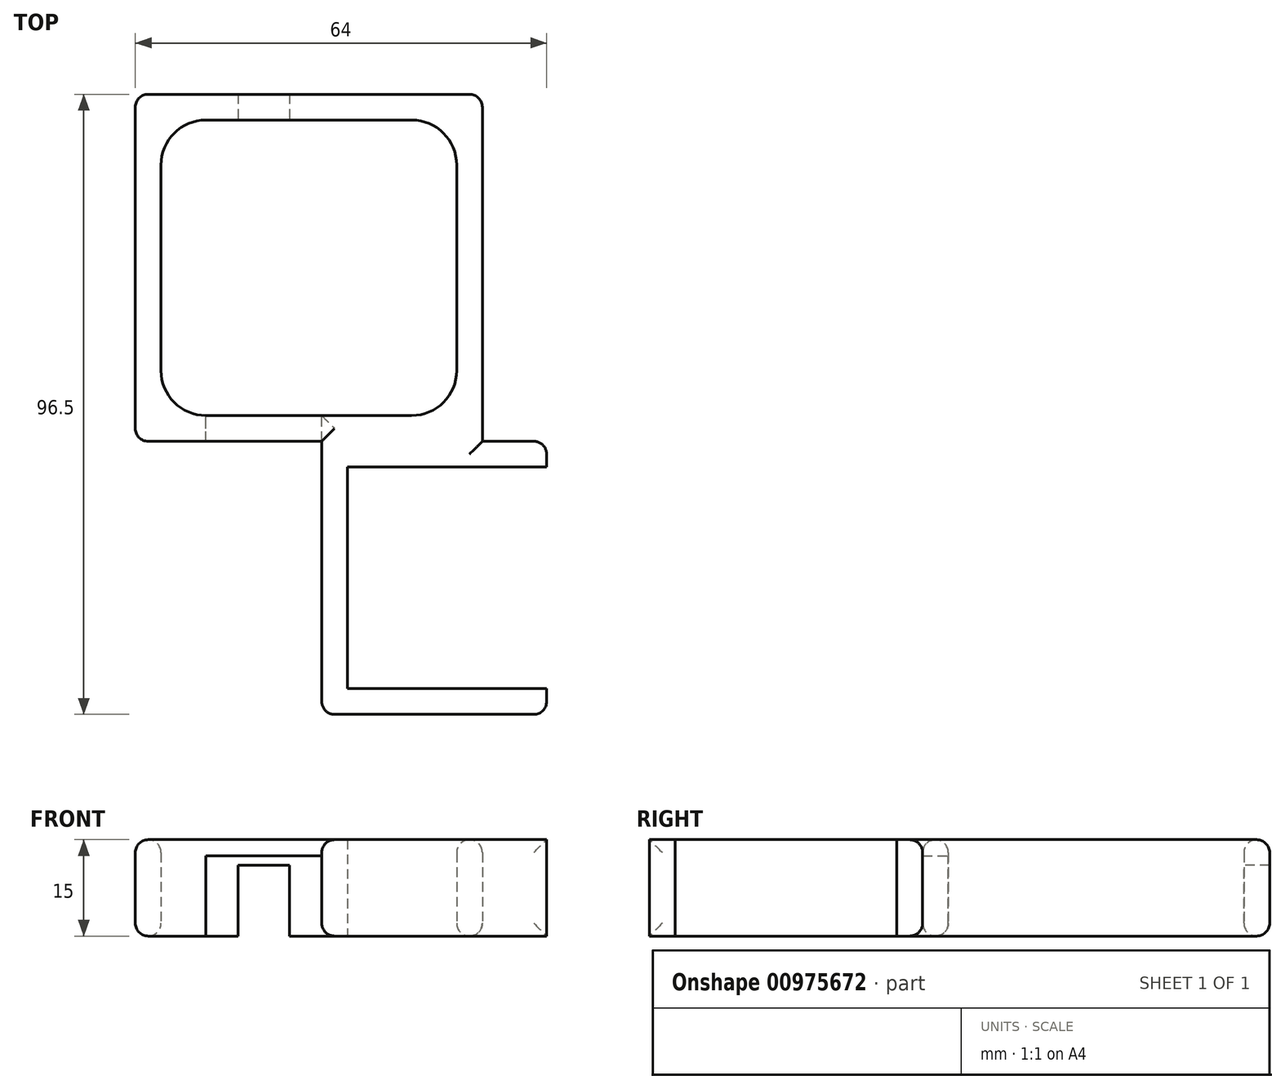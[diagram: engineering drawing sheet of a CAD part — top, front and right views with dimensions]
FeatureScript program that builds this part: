
annotation { "Feature Type Name" : "Feature", "Feature Type Description" : "" }
export const myFeature = defineFeature(function(context is Context, id is Id, definition is map)
    precondition{}
    {
        {
            var Q0;
            Q0=qCreatedBy(makeId("Top.planeOp"),FACE);
            var sketch = newSketch(context, id + "F0", { "sketchPlane" : qUnion([Q0])});
            skLineSegment(sketch, "E0", {"start": v(29.47, 14.54) * mm, "end": v(29.47, 10.54) * mm});
            skLineSegment(sketch, "E1", {"start": v(29.47, 10.54) * mm, "end": v(-1.53, 10.54) * mm});
            skLineSegment(sketch, "E2", {"start": v(-1.53, 10.54) * mm, "end": v(-1.53, -23.96) * mm});
            skLineSegment(sketch, "E3", {"start": v(-1.53, -23.96) * mm, "end": v(29.47, -23.96) * mm});
            skLineSegment(sketch, "E4", {"start": v(29.47, -23.96) * mm, "end": v(29.47, -27.96) * mm});
            skLineSegment(sketch, "E5", {"start": v(29.47, -27.96) * mm, "end": v(-5.53, -27.96) * mm});
            skLineSegment(sketch, "E6", {"start": v(-5.53, -27.96) * mm, "end": v(-5.53, 14.54) * mm});
            skLineSegment(sketch, "E7", {"start": v(-5.53, 14.54) * mm, "end": v(29.47, 14.54) * mm});
            skLineSegment(sketch, "E8.bottom", {"start": v(29.47, -23.96) * mm, "end": v(27.47, -23.96) * mm});
            skLineSegment(sketch, "E9.bottom", {"start": v(29.47, 10.54) * mm, "end": v(27.47, 10.54) * mm});
            skPoint(sketch, "E10", {"position": v(-5.53, -6.71) * mm});
            skSolve(sketch);
        }
        {
            var Q0;
            Q0 = qSketchRegion(id + "F0", true);
            extrude(context, id + "F1", {"entities" : qUnion([Q0]), "endBound" : BoundingType.SYMMETRIC, "depth" : 15 * mm, "offsetDistance" : 25 * mm});
        }
        {
            var Q0;
            Q0=qCreatedBy(makeId("Top.planeOp"),FACE);
            var sketch = newSketch(context, id + "F2", { "sketchPlane" : qUnion([Q0])});
            skPoint(sketch, "E11.0", {"position": v(-5.53, 14.54) * mm});
            skPoint(sketch, "E12.0", {"position": v(29.47, 14.54) * mm});
            skLineSegment(sketch, "E13.bottom", {"start": v(-30.53, 64.54) * mm, "end": v(-18.53, 64.54) * mm});
            skLineSegment(sketch, "E13.top", {"start": v(-30.53, 18.54) * mm, "end": v(-23.53, 18.54) * mm});
            skLineSegment(sketch, "E13.left", {"start": v(-30.53, 64.54) * mm, "end": v(-30.53, 18.54) * mm});
            skLineSegment(sketch, "E13.right", {"start": v(15.47, 64.54) * mm, "end": v(15.47, 18.54) * mm});
            skLineSegment(sketch, "E14.0", {"start": v(-34.53, 68.54) * mm, "end": v(-18.53, 68.54) * mm});
            skLineSegment(sketch, "E14.1", {"start": v(-34.53, 68.54) * mm, "end": v(-34.53, 14.54) * mm});
            skLineSegment(sketch, "E14.2", {"start": v(-34.53, 14.54) * mm, "end": v(-23.53, 14.54) * mm});
            skLineSegment(sketch, "E14.3", {"start": v(19.47, 68.54) * mm, "end": v(19.47, 14.54) * mm});
            skLineSegment(sketch, "E15", {"start": v(-5.53, 14.54) * mm, "end": v(-5.53, 18.54) * mm});
            skLineSegment(sketch, "E16.MirrorCS", {"start": v(-23.53, 14.54) * mm, "end": v(-23.53, 18.54) * mm});
            skLineSegment(sketch, "E17", {"start": v(-18.53, 79.1) * mm, "end": v(-18.53, 29.22) * mm});
            skLineSegment(sketch, "E18", {"start": v(-10.53, 79.84) * mm, "end": v(-10.53, 54.16) * mm});
            skLineSegment(sketch, "E19.trimOffspring", {"start": v(-10.53, 68.54) * mm, "end": v(19.47, 68.54) * mm});
            skLineSegment(sketch, "E20.trimOffspring", {"start": v(-10.53, 64.54) * mm, "end": v(15.47, 64.54) * mm});
            skLineSegment(sketch, "E21.trimOffspring", {"start": v(-5.53, 18.54) * mm, "end": v(15.47, 18.54) * mm});
            skLineSegment(sketch, "E22.trimOffspring", {"start": v(-5.53, 14.54) * mm, "end": v(19.47, 14.54) * mm});
            skLineSegment(sketch, "E23", {"start": v(-23.53, 14.54) * mm, "end": v(-5.53, 14.54) * mm});
            skLineSegment(sketch, "E24", {"start": v(-23.53, 18.54) * mm, "end": v(-5.53, 18.54) * mm});
            skLineSegment(sketch, "E25", {"start": v(-18.53, 68.54) * mm, "end": v(-10.53, 68.54) * mm});
            skLineSegment(sketch, "E26", {"start": v(-10.53, 64.54) * mm, "end": v(-18.53, 64.54) * mm});
            skSolve(sketch);
        }
        {
            var Q0;
            {var subQ1=sQuery(id+"F2.wireOp",EDGE,"E13.bottom");Q0=makeQuery(id+"F2.imprint","IMPRINT",FACE,{"disambiguationData":[TD([[makeQuery(id+"F2.imprint","IMPRINT",EDGE,{"derivedFrom":subQ1}),1.0]])]});}
            var Q1;
            Q1=makeQuery(id+"F2.imprint","IMPRINT",FACE,{"disambiguationData":[TD([[makeQuery(id+"F2.imprint","IMPRINT",EDGE,{"derivedFrom":sQuery(id+"F2.wireOp",EDGE,"E13.right")}),1.0]])]});
            var Q2;
            Q2=makeQuery(id+"F2.imprint","IMPRINT",FACE,{"disambiguationData":[TD([[makeQuery(id+"F2.imprint","IMPRINT",EDGE,{"derivedFrom":sQuery(id+"F2.wireOp",EDGE,"E15")}),1.0]])]});
            var Q3;
            {var subQ2=sQuery(id+"F2.wireOp",EDGE,"E25");Q3=makeQuery(id+"F2.imprint","IMPRINT",FACE,{"disambiguationData":[TD([[makeQuery(id+"F2.imprint","IMPRINT",EDGE,{"derivedFrom":subQ2}),-1.0]])]});}
            extrude(context, id + "F3", {"entities" : qUnion([Q0, Q1, Q2, Q3]), "operationType" : NewBodyOperationType.ADD, "endBound" : BoundingType.SYMMETRIC, "depth" : 15 * mm, "offsetDistance" : 25 * mm});
        }
        {
            var Q0;
            Q0=makeQuery(id+"F2.imprint","IMPRINT",FACE,{"disambiguationData":[TD([[makeQuery(id+"F2.imprint","IMPRINT",EDGE,{"derivedFrom":sQuery(id+"F2.wireOp",EDGE,"E15")}),1.0]])]});
            extrude(context, id + "F4", {"entities" : qUnion([Q0]), "operationType" : NewBodyOperationType.REMOVE, "endBound" : BoundingType.SYMMETRIC, "oppositeDirection" : true, "depth" : 10 * mm, "offsetDistance" : 25 * mm});
        }
        {
            var Q0;
            Q0=makeQuery(id+"F2.imprint","IMPRINT",FACE,{"disambiguationData":[TD([[makeQuery(id+"F2.imprint","IMPRINT",EDGE,{"derivedFrom":sQuery(id+"F2.wireOp",EDGE,"E15")}),1.0]])]});
            extrude(context, id + "F5", {"entities" : qUnion([Q0]), "operationType" : NewBodyOperationType.REMOVE, "oppositeDirection" : true, "depth" : 25 * mm, "offsetDistance" : 25 * mm});
        }
        {
            var Q0;
            {var subQ2=sQuery(id+"F2.wireOp",EDGE,"E25");Q0=makeQuery(id+"F2.imprint","IMPRINT",FACE,{"disambiguationData":[TD([[makeQuery(id+"F2.imprint","IMPRINT",EDGE,{"derivedFrom":subQ2}),-1.0]])]});}
            extrude(context, id + "F6", {"entities" : qUnion([Q0]), "operationType" : NewBodyOperationType.REMOVE, "endBound" : BoundingType.SYMMETRIC, "oppositeDirection" : true, "depth" : 7 * mm, "offsetDistance" : 25 * mm});
        }
        {
            var Q0;
            {var subQ2=sQuery(id+"F2.wireOp",EDGE,"E25");Q0=makeQuery(id+"F2.imprint","IMPRINT",FACE,{"disambiguationData":[TD([[makeQuery(id+"F2.imprint","IMPRINT",EDGE,{"derivedFrom":subQ2}),-1.0]])]});}
            extrude(context, id + "F7", {"entities" : qUnion([Q0]), "operationType" : NewBodyOperationType.REMOVE, "oppositeDirection" : true, "depth" : 25 * mm, "offsetDistance" : 25 * mm});
        }
        {
            var Q0;
            Q0=makeQuery(id+"F3.opExtrude","SWEPT_EDGE",EDGE,{"disambiguationData":[OSD([sQuery(id+"F2.wireOp",EDGE,"E13.bottom"),sQuery(id+"F2.wireOp",EDGE,"E13.left")])]});
            var Q1;
            Q1=makeQuery(id+"F3.opExtrude","SWEPT_EDGE",EDGE,{"disambiguationData":[OSD([sQuery(id+"F2.wireOp",EDGE,"E13.right"),sQuery(id+"F2.wireOp",EDGE,"E20.trimOffspring")])]});
            var Q2;
            Q2=makeQuery(id+"F3.opExtrude","SWEPT_EDGE",EDGE,{"disambiguationData":[OSD([sQuery(id+"F2.wireOp",EDGE,"E13.top"),sQuery(id+"F2.wireOp",EDGE,"E13.left")])]});
            var Q3;
            Q3=makeQuery(id+"F3.opExtrude","SWEPT_EDGE",EDGE,{"disambiguationData":[OSD([sQuery(id+"F2.wireOp",EDGE,"E13.right"),sQuery(id+"F2.wireOp",EDGE,"E21.trimOffspring")])]});
            fillet(context, id + "F8", {"entities" : qUnion([Q0, Q1, Q2, Q3]), "radius" : 7 * mm, "tangentPropagation" : true, "defaultsChanged" : true, "vertexSettings" : [], "allowEdgeOverflow" : false});
        }
        {
            var Q0;
            Q0=makeQuery(id+"F3.opExtrude","CAP_EDGE",EDGE,{"disambiguationData":[OSD([sQuery(id+"F2.wireOp",EDGE,"E14.3")])],"isStart":false});
            var Q1;
            Q1=makeQuery(id+"F3.opExtrude","CAP_EDGE",EDGE,{"disambiguationData":[OSD([sQuery(id+"F2.wireOp",EDGE,"E14.3")])],"isStart":true});
            var Q2;
            Q2=makeQuery(id+"F1.opExtrude","CAP_EDGE",EDGE,{"disambiguationData":[OSD([sQuery(id+"F0.wireOp",EDGE,"E7")])],"isStart":false});
            var Q3;
            Q3=makeQuery(id+"F1.opExtrude","CAP_EDGE",EDGE,{"disambiguationData":[OSD([sQuery(id+"F0.wireOp",EDGE,"E7")])],"isStart":true});
            var Q4;
            Q4=makeQuery(id+"F3.opExtrude","SWEPT_EDGE",EDGE,{"disambiguationData":[OSD([sQuery(id+"F2.wireOp",EDGE,"E14.3"),sQuery(id+"F2.wireOp",EDGE,"E19.trimOffspring")])]});
            var Q5;
            {var subQ0=sQuery(id+"F2.wireOp",EDGE,"E14.3");var subQ2=sQuery(id+"F2.wireOp",EDGE,"E25");var subQ3=sQuery(id+"F2.wireOp",EDGE,"E19.trimOffspring");var subQ4=sQuery(id+"F2.wireOp",EDGE,"E14.0");Q5=makeQuery(id+"F7.boolean.opBoolean","SPLIT",EDGE,{"disambiguationData":[TD([makeQuery(id+"F3.opExtrude","SWEPT_FACE",FACE,{"disambiguationData":[OSD([subQ0])]})])],"derivedFrom":makeQuery(id+"F3.opExtrude","CAP_EDGE",EDGE,{"disambiguationData":[OSD([subQ4,subQ3,subQ2])],"isStart":true})});}
            var Q6;
            Q6=makeQuery(id+"F3.opExtrude","CAP_EDGE",EDGE,{"disambiguationData":[OSD([sQuery(id+"F2.wireOp",EDGE,"E14.0"),sQuery(id+"F2.wireOp",EDGE,"E19.trimOffspring"),sQuery(id+"F2.wireOp",EDGE,"E25")])],"isStart":false});
            var Q7;
            Q7=makeQuery(id+"F6.boolean.opBoolean","COPY",EDGE,{"derivedFrom":makeQuery(id+"F6.opExtrude","CAP_EDGE",EDGE,{"disambiguationData":[OSD([sQuery(id+"F2.wireOp",EDGE,"E25")])],"isStart":true})});
            var Q8;
            {var subQ0=sQuery(id+"F2.wireOp",EDGE,"E25");var subQ1=sQuery(id+"F2.wireOp",EDGE,"E17");var subQ2=sQuery(id+"F2.wireOp",EDGE,"E14.0");Q8=makeQuery(id+"F7.boolean.opBoolean","MERGE",EDGE,{"derivedFrom":[makeQuery(id+"F6.boolean.opBoolean","COPY",EDGE,{"derivedFrom":makeQuery(id+"F6.opExtrude","SWEPT_EDGE",EDGE,{"disambiguationData":[OSD([subQ2,subQ1,subQ0])]})})],"fromTools":[makeQuery(id+"F7.opExtrude","SWEPT_EDGE",EDGE,{"disambiguationData":[OSD([subQ2,subQ1,subQ0])]})]});}
            var Q9;
            {var subQ0=sQuery(id+"F2.wireOp",EDGE,"E25");var subQ1=sQuery(id+"F2.wireOp",EDGE,"E19.trimOffspring");var subQ2=sQuery(id+"F2.wireOp",EDGE,"E18");Q9=makeQuery(id+"F7.boolean.opBoolean","MERGE",EDGE,{"derivedFrom":[makeQuery(id+"F6.boolean.opBoolean","COPY",EDGE,{"derivedFrom":makeQuery(id+"F6.opExtrude","SWEPT_EDGE",EDGE,{"disambiguationData":[OSD([subQ2,subQ1,subQ0])]})})],"fromTools":[makeQuery(id+"F7.opExtrude","SWEPT_EDGE",EDGE,{"disambiguationData":[OSD([subQ2,subQ1,subQ0])]})]});}
            var Q10;
            {var subQ0=sQuery(id+"F2.wireOp",EDGE,"E26");var subQ1=sQuery(id+"F2.wireOp",EDGE,"E20.trimOffspring");var subQ2=sQuery(id+"F2.wireOp",EDGE,"E18");Q10=makeQuery(id+"F7.boolean.opBoolean","MERGE",EDGE,{"derivedFrom":[makeQuery(id+"F6.boolean.opBoolean","COPY",EDGE,{"derivedFrom":makeQuery(id+"F6.opExtrude","SWEPT_EDGE",EDGE,{"disambiguationData":[OSD([subQ2,subQ1,subQ0])]})})],"fromTools":[makeQuery(id+"F7.opExtrude","SWEPT_EDGE",EDGE,{"disambiguationData":[OSD([subQ2,subQ1,subQ0])]})]});}
            var Q11;
            {var subQ0=sQuery(id+"F2.wireOp",EDGE,"E26");var subQ1=sQuery(id+"F2.wireOp",EDGE,"E17");var subQ2=sQuery(id+"F2.wireOp",EDGE,"E13.bottom");Q11=makeQuery(id+"F7.boolean.opBoolean","MERGE",EDGE,{"derivedFrom":[makeQuery(id+"F6.boolean.opBoolean","COPY",EDGE,{"derivedFrom":makeQuery(id+"F6.opExtrude","SWEPT_EDGE",EDGE,{"disambiguationData":[OSD([subQ2,subQ1,subQ0])]})})],"fromTools":[makeQuery(id+"F7.opExtrude","SWEPT_EDGE",EDGE,{"disambiguationData":[OSD([subQ2,subQ1,subQ0])]})]});}
            var Q12;
            Q12=makeQuery(id+"F3.opExtrude","SWEPT_EDGE",EDGE,{"disambiguationData":[OSD([sQuery(id+"F2.wireOp",EDGE,"E14.0"),sQuery(id+"F2.wireOp",EDGE,"E14.1")])]});
            var Q13;
            {var subQ0=sQuery(id+"F2.wireOp",EDGE,"E14.1");var subQ1=sQuery(id+"F2.wireOp",EDGE,"E25");var subQ2=sQuery(id+"F2.wireOp",EDGE,"E19.trimOffspring");var subQ3=sQuery(id+"F2.wireOp",EDGE,"E14.0");Q13=makeQuery(id+"F7.boolean.opBoolean","SPLIT",EDGE,{"disambiguationData":[TD([makeQuery(id+"F3.opExtrude","SWEPT_FACE",FACE,{"disambiguationData":[OSD([subQ0])]})])],"derivedFrom":makeQuery(id+"F3.opExtrude","CAP_EDGE",EDGE,{"disambiguationData":[OSD([subQ3,subQ2,subQ1])],"isStart":true})});}
            var Q14;
            Q14=makeQuery(id+"F3.opExtrude","CAP_EDGE",EDGE,{"disambiguationData":[OSD([sQuery(id+"F2.wireOp",EDGE,"E13.left")])],"isStart":true});
            var Q15;
            Q15=makeQuery(id+"F3.opExtrude","CAP_EDGE",EDGE,{"disambiguationData":[OSD([sQuery(id+"F2.wireOp",EDGE,"E13.right")])],"isStart":true});
            var Q16;
            Q16=makeQuery(id+"F3.opExtrude","CAP_EDGE",EDGE,{"disambiguationData":[OSD([sQuery(id+"F2.wireOp",EDGE,"E14.1")])],"isStart":true});
            var Q17;
            Q17=makeQuery(id+"F3.opExtrude","CAP_EDGE",EDGE,{"disambiguationData":[OSD([sQuery(id+"F2.wireOp",EDGE,"E14.2"),sQuery(id+"F2.wireOp",EDGE,"E22.trimOffspring"),sQuery(id+"F2.wireOp",EDGE,"E23")])],"isStart":true});
            var Q18;
            Q18=makeQuery(id+"F3.opExtrude","CAP_EDGE",EDGE,{"disambiguationData":[OSD([sQuery(id+"F2.wireOp",EDGE,"E14.1")])],"isStart":false});
            var Q19;
            Q19=makeQuery(id+"F3.opExtrude","CAP_EDGE",EDGE,{"disambiguationData":[OSD([sQuery(id+"F2.wireOp",EDGE,"E14.2"),sQuery(id+"F2.wireOp",EDGE,"E22.trimOffspring"),sQuery(id+"F2.wireOp",EDGE,"E23")])],"isStart":false});
            var Q20;
            Q20=makeQuery(id+"F3.opExtrude","CAP_EDGE",EDGE,{"disambiguationData":[OSD([sQuery(id+"F2.wireOp",EDGE,"E13.left")])],"isStart":false});
            var Q21;
            {var subQ0=sQuery(id+"F2.wireOp",EDGE,"E24");var subQ1=sQuery(id+"F2.wireOp",EDGE,"E16.MirrorCS");var subQ2=sQuery(id+"F2.wireOp",EDGE,"E13.top");Q21=makeQuery(id+"F5.boolean.opBoolean","MERGE",EDGE,{"derivedFrom":[makeQuery(id+"F4.boolean.opBoolean","COPY",EDGE,{"derivedFrom":makeQuery(id+"F4.opExtrude","SWEPT_EDGE",EDGE,{"disambiguationData":[OSD([subQ2,subQ1,subQ0])]})})],"fromTools":[makeQuery(id+"F5.opExtrude","SWEPT_EDGE",EDGE,{"disambiguationData":[OSD([subQ2,subQ1,subQ0])]})]});}
            var Q22;
            {var subQ0=sQuery(id+"F2.wireOp",EDGE,"E23");var subQ1=sQuery(id+"F2.wireOp",EDGE,"E16.MirrorCS");var subQ2=sQuery(id+"F2.wireOp",EDGE,"E14.2");Q22=makeQuery(id+"F5.boolean.opBoolean","MERGE",EDGE,{"derivedFrom":[makeQuery(id+"F4.boolean.opBoolean","COPY",EDGE,{"derivedFrom":makeQuery(id+"F4.opExtrude","SWEPT_EDGE",EDGE,{"disambiguationData":[OSD([subQ2,subQ1,subQ0])]})})],"fromTools":[makeQuery(id+"F5.opExtrude","SWEPT_EDGE",EDGE,{"disambiguationData":[OSD([subQ2,subQ1,subQ0])]})]});}
            var Q23;
            {var subQ0=sQuery(id+"F2.wireOp",EDGE,"E24");var subQ1=sQuery(id+"F2.wireOp",EDGE,"E21.trimOffspring");var subQ2=sQuery(id+"F2.wireOp",EDGE,"E15");Q23=makeQuery(id+"F5.boolean.opBoolean","MERGE",EDGE,{"derivedFrom":[makeQuery(id+"F4.boolean.opBoolean","COPY",EDGE,{"derivedFrom":makeQuery(id+"F4.opExtrude","SWEPT_EDGE",EDGE,{"disambiguationData":[OSD([subQ2,subQ1,subQ0])]})})],"fromTools":[makeQuery(id+"F5.opExtrude","SWEPT_EDGE",EDGE,{"disambiguationData":[OSD([subQ2,subQ1,subQ0])]})]});}
            var Q24;
            Q24=makeQuery(id+"F5.boolean.opBoolean","INTERSECT",EDGE,{"derivedFrom":[makeQuery(id+"F3.boolean.opBoolean","MERGE",FACE,{"derivedFrom":[makeQuery(id+"F1.opExtrude","CAP_FACE",FACE,{"disambiguationData":[OSD([sQuery(id+"F0.wireOp",EDGE,"E0"),sQuery(id+"F0.wireOp",EDGE,"E1"),sQuery(id+"F0.wireOp",EDGE,"E2"),sQuery(id+"F0.wireOp",EDGE,"E3"),sQuery(id+"F0.wireOp",EDGE,"E4"),sQuery(id+"F0.wireOp",EDGE,"E5"),sQuery(id+"F0.wireOp",EDGE,"E6"),sQuery(id+"F0.wireOp",EDGE,"E7"),sQuery(id+"F0.wireOp",EDGE,"E8.bottom"),sQuery(id+"F0.wireOp",EDGE,"E9.bottom")])],"isStart":true}),makeQuery(id+"F3.opExtrude","CAP_FACE",FACE,{"disambiguationData":[OSD([sQuery(id+"F2.wireOp",EDGE,"E13.bottom"),sQuery(id+"F2.wireOp",EDGE,"E13.top"),sQuery(id+"F2.wireOp",EDGE,"E13.left"),sQuery(id+"F2.wireOp",EDGE,"E13.right"),sQuery(id+"F2.wireOp",EDGE,"E14.0"),sQuery(id+"F2.wireOp",EDGE,"E14.1"),sQuery(id+"F2.wireOp",EDGE,"E14.2"),sQuery(id+"F2.wireOp",EDGE,"E14.3"),sQuery(id+"F2.wireOp",EDGE,"E19.trimOffspring"),sQuery(id+"F2.wireOp",EDGE,"E20.trimOffspring"),sQuery(id+"F2.wireOp",EDGE,"E21.trimOffspring"),sQuery(id+"F2.wireOp",EDGE,"E22.trimOffspring"),sQuery(id+"F2.wireOp",EDGE,"E23"),sQuery(id+"F2.wireOp",EDGE,"E24"),sQuery(id+"F2.wireOp",EDGE,"E25"),sQuery(id+"F2.wireOp",EDGE,"E26")])],"isStart":true})]}),makeQuery(id+"F5.opExtrude","SWEPT_FACE",FACE,{"disambiguationData":[OSD([sQuery(id+"F2.wireOp",EDGE,"E15")])]})]});
            var Q25;
            Q25=makeQuery(id+"F1.opExtrude","CAP_EDGE",EDGE,{"disambiguationData":[OSD([sQuery(id+"F0.wireOp",EDGE,"E6")])],"isStart":false});
            var Q26;
            Q26=makeQuery(id+"F1.opExtrude","SWEPT_EDGE",EDGE,{"disambiguationData":[OSD([sQuery(id+"F0.wireOp",EDGE,"E4"),sQuery(id+"F0.wireOp",EDGE,"E5")])]});
            var Q27;
            Q27=makeQuery(id+"F1.opExtrude","SWEPT_EDGE",EDGE,{"disambiguationData":[OSD([sQuery(id+"F0.wireOp",EDGE,"E5"),sQuery(id+"F0.wireOp",EDGE,"E6")])]});
            var Q28;
            Q28=makeQuery(id+"F3.opExtrude","SWEPT_EDGE",EDGE,{"disambiguationData":[OSD([sQuery(id+"F2.wireOp",EDGE,"E14.1"),sQuery(id+"F2.wireOp",EDGE,"E14.2")])]});
            var Q29;
            Q29=makeQuery(id+"F1.opExtrude","SWEPT_EDGE",EDGE,{"disambiguationData":[OSD([sQuery(id+"F0.wireOp",EDGE,"E0"),sQuery(id+"F0.wireOp",EDGE,"E7")])]});
            fillet(context, id + "F9", {"entities" : qUnion([Q0, Q1, Q2, Q3, Q4, Q5, Q6, Q7, Q8, Q9, Q10, Q11, Q12, Q13, Q14, Q15, Q16, Q17, Q18, Q19, Q20, Q21, Q22, Q23, Q24, Q25, Q26, Q27, Q28, Q29]), "radius" : 2 * mm, "tangentPropagation" : true, "allowEdgeOverflow" : false});
        }
    });
